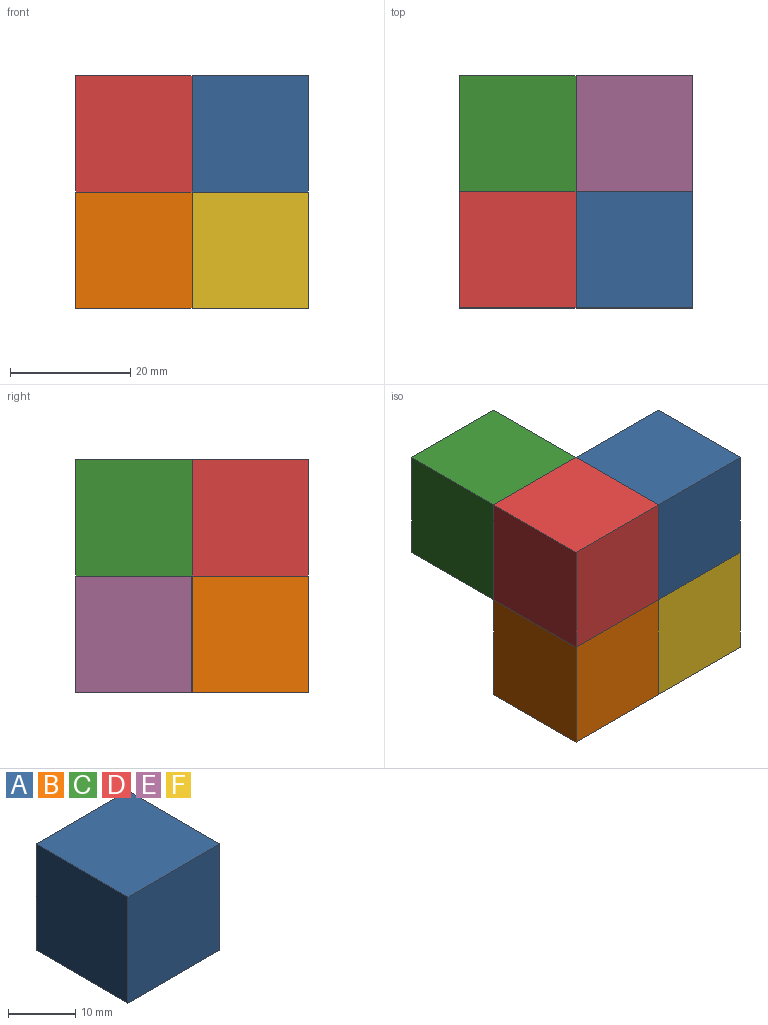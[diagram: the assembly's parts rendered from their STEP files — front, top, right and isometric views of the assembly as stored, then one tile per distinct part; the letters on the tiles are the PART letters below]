
ASSEMBLY  parts=6 mates=5
PART A: 6 faces, bbox 19.3x19.3x19.3 mm
  f0: plane 19.3x19.3mm, normal (0,0,1), area 372.6mm2, adj f1,f3,f4,f5
  f1: plane 19.3x19.3mm, normal (-1,0,0), area 372.6mm2, adj f0,f2,f4,f5
  f2: plane 19.3x19.3mm, normal (0,0,-1), area 372.6mm2, adj f1,f3,f4,f5
  f3: plane 19.3x19.3mm, normal (1,0,0), area 372.6mm2, adj f0,f2,f4,f5
  f4: plane 19.3x19.3mm, normal (0,-1,0), area 372.6mm2, adj f0,f1,f2,f3
  f5: plane 19.3x19.3mm, normal (0,1,0), area 372.6mm2, adj f0,f1,f2,f3
PART B: same geometry as A
PART C: same geometry as A
PART D: same geometry as A
PART E: same geometry as A
PART F: same geometry as A
PLACE A t=(-59.78,-59.82,-4.18)mm
PLACE B t=(-79.09,-59.82,-23.48)mm
PLACE C t=(-79.09,-40.52,-4.18)mm
PLACE D t=(-79.09,-59.82,-4.18)mm
PLACE E t=(-59.78,-40.52,-23.48)mm
PLACE F t=(-59.78,-59.82,-23.48)mm
MATE fastened B.f0 <-> D.f2  axis (0,0,1) through (-79.09,-69.48,-13.83)mm
MATE fastened F.f5 <-> E.f4  axis (0,1,0) through (-59.78,-59.82,-23.48)mm
MATE fastened B.f3 <-> F.f1  axis (1,0,0) through (-69.43,-69.48,-23.48)mm
MATE fastened D.f5 <-> C.f4  axis (0,1,0) through (-79.09,-59.82,-4.18)mm
MATE fastened F.f0 <-> A.f2  axis (0,0,1) through (-59.78,-69.48,-13.83)mm
